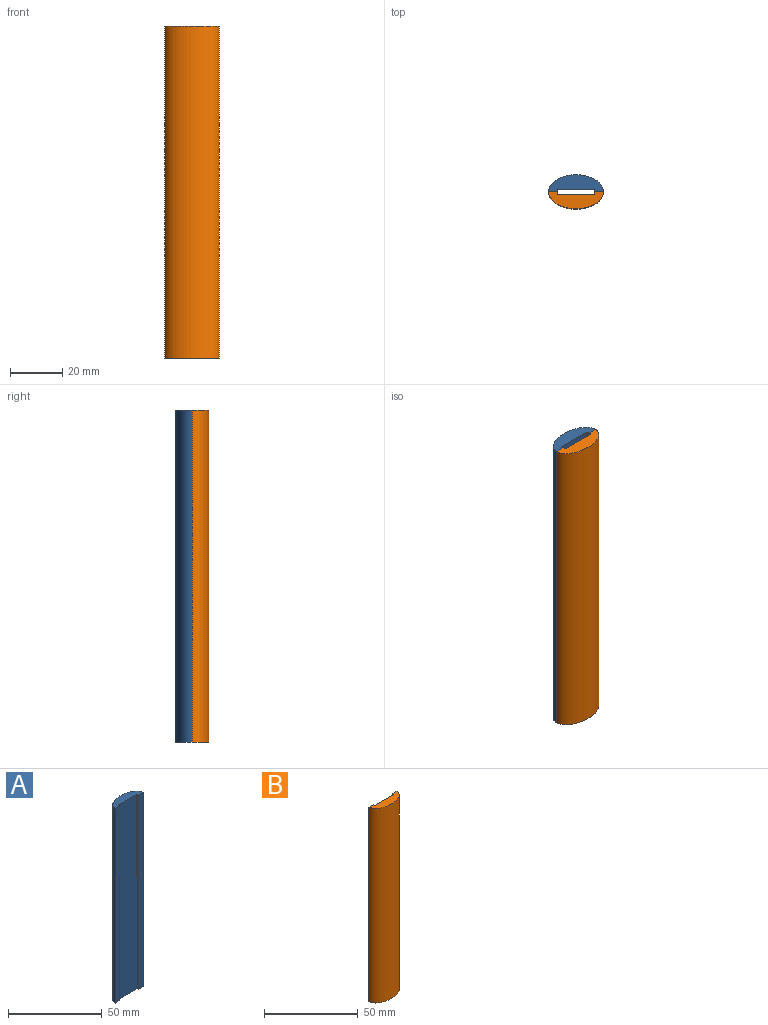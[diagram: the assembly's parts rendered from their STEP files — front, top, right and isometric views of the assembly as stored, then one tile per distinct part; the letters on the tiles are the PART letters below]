
ASSEMBLY  parts=2 mates=1
PART A: 10 faces, bbox 21x13x127 mm
  f0: plane 127x3.5mm, normal (0,-1,0), area 444.5mm2, adj f1,f2,f3,f9
  f1: plane 21x6.5mm, normal (0,0,1), area 93.2mm2, adj f0,f3,f4,f5,f6,f7,f8,f9
  f2: plane 21x6.5mm, normal (0,0,-1), area 93.2mm2, adj f0,f3,f4,f5,f6,f7,f8,f9
  f3: bspline ~127x21mm, area 3438.4mm2, adj f0,f1,f2,f4
  f4: plane 127x3.5mm, normal (0,-1,0), area 444.5mm2, adj f1,f2,f3,f5
  f5: plane 127x0.8mm, normal (-1,0,0), area 101.6mm2, adj f1,f2,f4,f6
  f6: cylinder r=0.2mm len=127mm, axis (0,0,1), area 39.9mm2, adj f1,f2,f5,f7
  f7: plane 127x13.6mm, normal (0,-1,0), area 1727.2mm2, adj f1,f2,f6,f8
  f8: cylinder r=0.2mm len=127mm, axis (0,0,1), area 39.9mm2, adj f1,f2,f7,f9
  f9: plane 127x0.8mm, normal (1,0,0), area 101.6mm2, adj f0,f1,f2,f8
PART B: 10 faces, bbox 21x13x127 mm
  f0: plane 127x3.5mm, normal (0,1,0), area 444.5mm2, adj f1,f2,f3,f9
  f1: plane 21x6.5mm, normal (0,0,1), area 93.2mm2, adj f0,f3,f4,f5,f6,f7,f8,f9
  f2: plane 21x6.5mm, normal (0,0,-1), area 93.2mm2, adj f0,f3,f4,f5,f6,f7,f8,f9
  f3: bspline ~127x21mm, area 3438.4mm2, adj f0,f1,f2,f4
  f4: plane 127x3.5mm, normal (0,1,0), area 444.5mm2, adj f1,f2,f3,f5
  f5: plane 127x0.8mm, normal (-1,0,0), area 101.6mm2, adj f1,f2,f4,f6
  f6: cylinder r=0.2mm len=127mm, axis (0,0,1), area 39.9mm2, adj f1,f2,f5,f7
  f7: plane 127x13.6mm, normal (0,1,0), area 1727.2mm2, adj f1,f2,f6,f8
  f8: cylinder r=0.2mm len=127mm, axis (0,0,1), area 39.9mm2, adj f1,f2,f7,f9
  f9: plane 127x0.8mm, normal (1,0,0), area 101.6mm2, adj f0,f1,f2,f8
PLACE A t=(-56.81,-58.99,19.33)mm
PLACE B t=(-56.81,-58.99,19.33)mm
MATE fastened A.f0 <-> B.f0  axis (0,-1,0) through (-67.31,-58.99,19.33)mm
